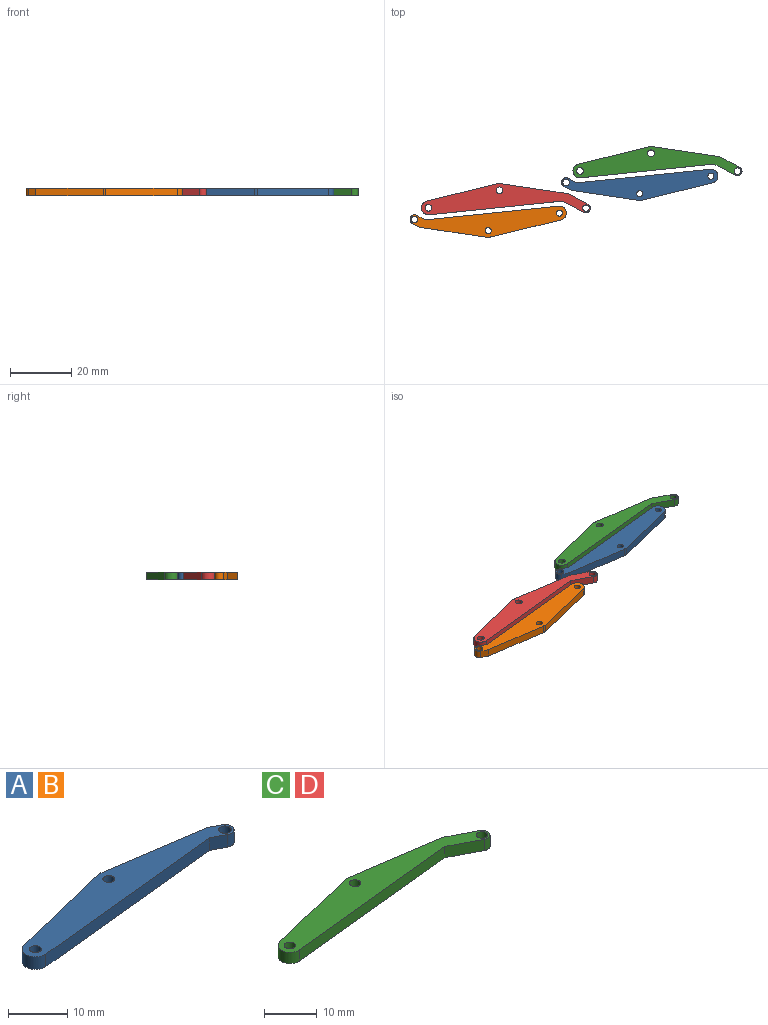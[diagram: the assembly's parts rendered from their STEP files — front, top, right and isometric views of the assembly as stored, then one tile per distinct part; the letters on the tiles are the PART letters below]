
ASSEMBLY  parts=4 mates=1
PART A: 13 faces, bbox 51.1x10.2x2.6 mm
  f0: cylinder r=2.21mm len=2.6mm, axis (0,0,-1), area 2.2mm2, adj f1,f8,f11,f12
  f1: plane 23.27x5.68mm, normal (-0.24,0.97,0), area 62.3mm2, adj f0,f2,f11,f12
  f2: cylinder r=2.28mm len=4.5mm, axis (0,0,-1), area 17.8mm2, adj f1,f3,f11,f12
  f3: plane 43.59x4.49mm, normal (0.1,-0.99,0), area 113.9mm2, adj f2,f4,f11,f12
  f4: plane 2.84x2.6mm, normal (-0.46,-0.89,0), area 8.3mm2, adj f3,f5,f11,f12
  f5: cylinder r=1.5mm len=2.83mm, axis (0,0,-1), area 12.3mm2, adj f4,f6,f11,f12
  f6: plane 2.6x2.38mm, normal (0.46,0.89,0), area 7mm2, adj f5,f8,f11,f12
  f7: cylinder r=1mm len=2.6mm, axis (0,0,-1), area 16.3mm2, adj f11,f12
  f8: plane 22.09x3.29mm, normal (0.15,0.99,0), area 58.1mm2, adj f0,f6,f11,f12
  f9: cylinder r=1mm len=2.6mm, axis (0,0,-1), area 16.3mm2, adj f11,f12
  f10: cylinder r=1.07mm len=2.6mm, axis (0,0,-1), area 17.6mm2, adj f11,f12
  f11: plane 51.14x10.24mm, normal (0,0,1), area 267.9mm2, adj f0,f1,f2,f3,f4,f5,f6,f7
  f12: plane 51.14x10.24mm, normal (0,0,-1), area 267.9mm2, adj f0,f1,f2,f3,f4,f5,f6,f7
PART B: same geometry as A
PART C: 13 faces, bbox 55.3x10.2x2.6 mm
  f0: cylinder r=2.21mm len=2.6mm, axis (0,0,-1), area 2.2mm2, adj f1,f8,f11,f12
  f1: plane 23.27x5.68mm, normal (-0.24,0.97,0), area 62.3mm2, adj f0,f2,f11,f12
  f2: cylinder r=2.28mm len=4.5mm, axis (0,0,-1), area 17.8mm2, adj f1,f3,f11,f12
  f3: plane 43.59x4.49mm, normal (0.1,-0.99,0), area 113.9mm2, adj f2,f4,f11,f12
  f4: plane 6.97x3.65mm, normal (-0.46,-0.89,0), area 20.5mm2, adj f3,f5,f11,f12
  f5: cylinder r=1.5mm len=2.83mm, axis (0,0,-1), area 12.3mm2, adj f4,f6,f11,f12
  f6: plane 6.52x3.41mm, normal (0.46,0.89,0), area 19.1mm2, adj f5,f8,f11,f12
  f7: cylinder r=1.1mm len=2.6mm, axis (0,0,-1), area 18mm2, adj f11,f12
  f8: plane 22.09x3.29mm, normal (0.15,0.99,0), area 58.1mm2, adj f0,f6,f11,f12
  f9: cylinder r=1.1mm len=2.6mm, axis (0,0,-1), area 18mm2, adj f11,f12
  f10: cylinder r=1.07mm len=2.6mm, axis (0,0,-1), area 17.6mm2, adj f11,f12
  f11: plane 55.27x10.24mm, normal (0,0,1), area 280.6mm2, adj f0,f1,f2,f3,f4,f5,f6,f7
  f12: plane 55.27x10.24mm, normal (0,0,-1), area 280.6mm2, adj f0,f1,f2,f3,f4,f5,f6,f7
PART D: same geometry as C
PLACE A rot(axis=(0,0,1),180deg) t=(-10.45,-5.73,0.64)mm
PLACE B rot(axis=(0,0,1),180deg) t=(-60,-17.81,0.64)mm
PLACE C rot(axis=(0,0,-1),0deg) t=(-4.38,1.37,0.64)mm
PLACE D rot(axis=(0,0,-1),0deg) t=(-53.92,-10.71,0.64)mm
MATE planar C.f11 <-> A.f11  axis (0,0,1) through (-5.95,1.42,1.94)mm
